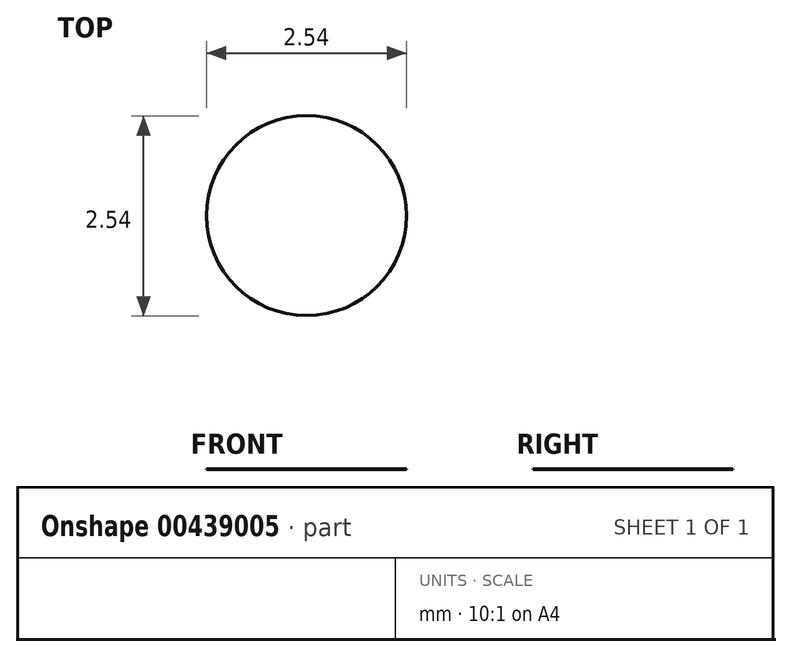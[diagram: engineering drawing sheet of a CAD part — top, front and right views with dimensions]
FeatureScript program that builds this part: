
annotation { "Feature Type Name" : "Feature", "Feature Type Description" : "" }
export const myFeature = defineFeature(function(context is Context, id is Id, definition is map)
    precondition{}
    {
        {
            var Q0;
            Q0=qCreatedBy(makeId("Top.planeOp"),FACE);
            var sketch = newSketch(context, id + "F0", { "sketchPlane" : qUnion([Q0])});
            skCircle(sketch, "E0.cCircle", {"center": v(0, 0) * mm, "radius": 44 * mm, "construction": true});
            skLineSegment(sketch, "E0.0", {"start": v(25.4, -44) * mm, "end": v(-25.4, -44) * mm});
            skLineSegment(sketch, "E0.1", {"start": v(-25.4, -44) * mm, "end": v(-50.8, 0) * mm});
            skLineSegment(sketch, "E0.2", {"start": v(-50.8, 0) * mm, "end": v(-25.4, 44) * mm, "construction": true});
            skLineSegment(sketch, "E0.3", {"start": v(-25.4, 44) * mm, "end": v(25.4, 44) * mm, "construction": true});
            skLineSegment(sketch, "E0.4", {"start": v(25.4, 44) * mm, "end": v(50.8, 0) * mm, "construction": true});
            skLineSegment(sketch, "E0.5", {"start": v(50.8, 0) * mm, "end": v(25.4, -44) * mm});
            skPoint(sketch, "E0.0.midPoint", {"position": v(0, -44) * mm});
            skCircle(sketch, "E1.cCircle", {"center": v(0, 87.99) * mm, "radius": 44 * mm, "construction": true});
            skLineSegment(sketch, "E1.0", {"start": v(25.4, 44) * mm, "end": v(-25.4, 44) * mm, "construction": true});
            skLineSegment(sketch, "E1.1", {"start": v(-25.4, 44) * mm, "end": v(-50.8, 87.99) * mm, "construction": true});
            skLineSegment(sketch, "E1.2", {"start": v(-50.8, 87.99) * mm, "end": v(-25.4, 131.98) * mm});
            skLineSegment(sketch, "E1.3", {"start": v(-25.4, 131.98) * mm, "end": v(25.4, 131.98) * mm});
            skLineSegment(sketch, "E1.4", {"start": v(25.4, 131.98) * mm, "end": v(50.8, 87.99) * mm});
            skLineSegment(sketch, "E1.5", {"start": v(50.8, 87.99) * mm, "end": v(25.4, 44) * mm, "construction": true});
            skPoint(sketch, "E1.0.midPoint", {"position": v(0, 44) * mm});
            skCircle(sketch, "E2.cCircle", {"center": v(76.2, 44) * mm, "radius": 44 * mm, "construction": true});
            skLineSegment(sketch, "E2.0", {"start": v(101.6, 0) * mm, "end": v(50.8, 0) * mm});
            skLineSegment(sketch, "E2.1", {"start": v(50.8, 0) * mm, "end": v(25.4, 44) * mm, "construction": true});
            skLineSegment(sketch, "E2.2", {"start": v(25.4, 44) * mm, "end": v(50.8, 87.99) * mm, "construction": true});
            skLineSegment(sketch, "E2.3", {"start": v(50.8, 87.99) * mm, "end": v(101.6, 87.99) * mm});
            skLineSegment(sketch, "E2.4", {"start": v(101.6, 87.99) * mm, "end": v(127, 44) * mm});
            skLineSegment(sketch, "E2.5", {"start": v(127, 44) * mm, "end": v(101.6, 0) * mm});
            skPoint(sketch, "E2.0.midPoint", {"position": v(76.2, 0) * mm});
            skCircle(sketch, "E3.cCircle", {"center": v(-76.2, 44) * mm, "radius": 44 * mm, "construction": true});
            skLineSegment(sketch, "E3.0", {"start": v(-50.8, 0) * mm, "end": v(-101.6, 0) * mm});
            skLineSegment(sketch, "E3.1", {"start": v(-101.6, 0) * mm, "end": v(-127, 44) * mm});
            skLineSegment(sketch, "E3.2", {"start": v(-127, 44) * mm, "end": v(-101.6, 87.99) * mm});
            skLineSegment(sketch, "E3.3", {"start": v(-101.6, 87.99) * mm, "end": v(-50.8, 87.99) * mm});
            skLineSegment(sketch, "E3.4", {"start": v(-50.8, 87.99) * mm, "end": v(-25.4, 44) * mm, "construction": true});
            skLineSegment(sketch, "E3.5", {"start": v(-25.4, 44) * mm, "end": v(-50.8, 0) * mm, "construction": true});
            skPoint(sketch, "E3.0.midPoint", {"position": v(-76.2, 0) * mm});
            skSolve(sketch);
        }
        {
            var Q0;
            Q0=makeQuery(id+"F0.imprint","IMPRINT",FACE,{"disambiguationData":[TD([[makeQuery(id+"F0.imprint","IMPRINT",EDGE,{"derivedFrom":sQuery(id+"F0.wireOp",EDGE,"E0.0")}),-1.0]])]});
            extrude(context, id + "F1", {"entities" : qUnion([Q0]), "depth" : 1 / 203.2 * mm});
        }
        {
            var Q0;
            Q0=makeQuery(id+"F1.opExtrude","CAP_FACE",FACE,{"disambiguationData":[OSD([sQuery(id+"F0.wireOp",EDGE,"E0.0"),sQuery(id+"F0.wireOp",EDGE,"E0.1"),sQuery(id+"F0.wireOp",EDGE,"E0.5"),sQuery(id+"F0.wireOp",EDGE,"E1.2"),sQuery(id+"F0.wireOp",EDGE,"E1.3"),sQuery(id+"F0.wireOp",EDGE,"E1.4"),sQuery(id+"F0.wireOp",EDGE,"E2.0"),sQuery(id+"F0.wireOp",EDGE,"E2.3"),sQuery(id+"F0.wireOp",EDGE,"E2.4"),sQuery(id+"F0.wireOp",EDGE,"E2.5"),sQuery(id+"F0.wireOp",EDGE,"E3.0"),sQuery(id+"F0.wireOp",EDGE,"E3.1"),sQuery(id+"F0.wireOp",EDGE,"E3.2"),sQuery(id+"F0.wireOp",EDGE,"E3.3")])],"isStart":false});
            var sketch = newSketch(context, id + "F2", { "sketchPlane" : qUnion([Q0])});
            skLineSegment(sketch, "E4", {"start": v(-50.8, 87.99) * mm, "end": v(-50.8, 0) * mm, "construction": true});
            skLineSegment(sketch, "E5", {"start": v(25.4, 131.98) * mm, "end": v(-25.4, 131.98) * mm, "construction": true});
            skPoint(sketch, "E6", {"position": v(-21.6, 69.4) * mm});
            skLineSegment(sketch, "E7.bottom", {"start": v(-20, 56.7) * mm, "end": v(-23.18, 56.7) * mm});
            skLineSegment(sketch, "E7.top", {"start": v(-20, 82.1) * mm, "end": v(-23.18, 82.1) * mm});
            skLineSegment(sketch, "E7.left", {"start": v(-20, 56.7) * mm, "end": v(-20, 82.1) * mm});
            skLineSegment(sketch, "E7.right", {"start": v(-23.18, 56.7) * mm, "end": v(-23.18, 82.1) * mm});
            skPoint(sketch, "E8", {"position": v(-21.59, 18.6) * mm});
            skLineSegment(sketch, "E9.bottom", {"start": v(-20, 5.9) * mm, "end": v(-23.18, 5.9) * mm});
            skLineSegment(sketch, "E9.top", {"start": v(-20, 31.3) * mm, "end": v(-23.18, 31.3) * mm});
            skLineSegment(sketch, "E9.left", {"start": v(-20, 5.9) * mm, "end": v(-20, 31.3) * mm});
            skLineSegment(sketch, "E9.right", {"start": v(-23.18, 5.9) * mm, "end": v(-23.18, 31.3) * mm});
            skLineSegment(sketch, "E10", {"start": v(0, 131.98) * mm, "end": v(0, -44) * mm, "construction": true});
            skLineSegment(sketch, "E11.MirrorCS", {"start": v(20, 82.1) * mm, "end": v(23.18, 82.1) * mm});
            skLineSegment(sketch, "E12.MirrorCS", {"start": v(20, 56.7) * mm, "end": v(20, 82.1) * mm});
            skLineSegment(sketch, "E13.MirrorCS", {"start": v(23.18, 56.7) * mm, "end": v(23.18, 82.1) * mm});
            skLineSegment(sketch, "E14.MirrorCS", {"start": v(20, 56.7) * mm, "end": v(23.18, 56.7) * mm});
            skLineSegment(sketch, "E15.MirrorCS", {"start": v(20, 31.3) * mm, "end": v(23.18, 31.3) * mm});
            skLineSegment(sketch, "E16.MirrorCS", {"start": v(20, 5.9) * mm, "end": v(20, 31.3) * mm});
            skLineSegment(sketch, "E17.MirrorCS", {"start": v(20, 5.9) * mm, "end": v(23.18, 5.9) * mm});
            skLineSegment(sketch, "E18.MirrorCS", {"start": v(23.18, 5.9) * mm, "end": v(23.18, 31.3) * mm});
            skPoint(sketch, "E19", {"position": v(-21.6, 44) * mm});
            skCircle(sketch, "E20", {"center": v(-21.6, 44) * mm, "radius": 1.27 * mm});
            skCircle(sketch, "E21.MirrorC", {"center": v(21.59, 44) * mm, "radius": 1.27 * mm});
            skLineSegment(sketch, "E22", {"start": v(-21.6, 131.98) * mm, "end": v(-21.59, -44) * mm, "construction": true});
            skLineSegment(sketch, "E23", {"start": v(99.38, 6.75) * mm, "end": v(99.38, 29.94) * mm, "construction": true});
            skSolve(sketch);
        }
        {
            var Q0;
            Q0=makeQuery(id+"F2.imprint","IMPRINT",FACE,{"disambiguationData":[TD([[makeQuery(id+"F2.imprint","IMPRINT",EDGE,{"derivedFrom":sQuery(id+"F2.wireOp",EDGE,"E7.bottom")}),-1.0]])]});
            var Q1;
            Q1=makeQuery(id+"F2.imprint","IMPRINT",FACE,{"disambiguationData":[TD([[makeQuery(id+"F2.imprint","IMPRINT",EDGE,{"derivedFrom":sQuery(id+"F2.wireOp",EDGE,"E11.MirrorCS")}),-1.0]])]});
            var Q2;
            Q2=makeQuery(id+"F2.imprint","IMPRINT",FACE,{"disambiguationData":[TD([[makeQuery(id+"F2.imprint","IMPRINT",EDGE,{"derivedFrom":sQuery(id+"F2.wireOp",EDGE,"E15.MirrorCS")}),-1.0]])]});
            var Q3;
            Q3=makeQuery(id+"F2.imprint","IMPRINT",FACE,{"disambiguationData":[TD([[makeQuery(id+"F2.imprint","IMPRINT",EDGE,{"derivedFrom":sQuery(id+"F2.wireOp",EDGE,"E9.bottom")}),-1.0]])]});
            extrude(context, id + "F3", {"entities" : qUnion([Q0, Q1, Q2, Q3]), "operationType" : NewBodyOperationType.REMOVE, "oppositeDirection" : true, "depth" : 7.62 * mm});
        }
        {
            var Q0;
            Q0=makeQuery(id+"F2.imprint","IMPRINT",FACE,{"disambiguationData":[TD([[makeQuery(id+"F2.imprint","IMPRINT",EDGE,{"derivedFrom":sQuery(id+"F2.wireOp",EDGE,"E20")}),1.0]])]});
            var Q1;
            Q1=makeQuery(id+"F2.imprint","IMPRINT",FACE,{"disambiguationData":[TD([[makeQuery(id+"F2.imprint","IMPRINT",EDGE,{"derivedFrom":sQuery(id+"F2.wireOp",EDGE,"E21.MirrorC")}),-1.0]])]});
            extrude(context, id + "F4", {"entities" : qUnion([Q0, Q1]), "operationType" : NewBodyOperationType.REMOVE, "oppositeDirection" : true, "depth" : 7.62 * mm});
        }
        {
            var Q0;
            Q0=makeQuery(id+"F2.imprint","IMPRINT",FACE,{"disambiguationData":[TD([[makeQuery(id+"F2.imprint","IMPRINT",EDGE,{"derivedFrom":sQuery(id+"F2.wireOp",EDGE,"E7.bottom")}),1.0]])]});
            var sketch = newSketch(context, id + "F5", { "sketchPlane" : qUnion([Q0])});
            skCircle(sketch, "E24", {"center": v(97.8, 21.95) * mm, "radius": 2.15 * mm});
            skPoint(sketch, "E25.0", {"position": v(21.59, 44) * mm});
            skPoint(sketch, "E26.0", {"position": v(127, 44) * mm});
            skLineSegment(sketch, "E27", {"start": v(21.59, 44) * mm, "end": v(127, 44) * mm, "construction": true});
            skCircle(sketch, "E28.MirrorC", {"center": v(97.8, 66.04) * mm, "radius": 2.15 * mm});
            skPoint(sketch, "E29.0", {"position": v(0, -44) * mm});
            skPoint(sketch, "E29.1", {"position": v(0, 131.98) * mm});
            skLineSegment(sketch, "E30", {"start": v(0, -44) * mm, "end": v(0, 131.98) * mm, "construction": true});
            skCircle(sketch, "E31.MirrorC", {"center": v(-97.8, 66.04) * mm, "radius": 2.15 * mm});
            skSolve(sketch);
        }
        {
            var Q0;
            Q0=makeQuery(id+"F5.imprint","IMPRINT",FACE,{"disambiguationData":[TD([[makeQuery(id+"F5.imprint","IMPRINT",EDGE,{"derivedFrom":sQuery(id+"F5.wireOp",EDGE,"E28.MirrorC")}),-1.0]])]});
            var Q1;
            Q1=makeQuery(id+"F5.imprint","IMPRINT",FACE,{"disambiguationData":[TD([[makeQuery(id+"F5.imprint","IMPRINT",EDGE,{"derivedFrom":sQuery(id+"F5.wireOp",EDGE,"E31.MirrorC")}),1.0]])]});
            extrude(context, id + "F6", {"entities" : qUnion([Q0, Q1]), "operationType" : NewBodyOperationType.REMOVE, "oppositeDirection" : true, "depth" : 25.4 * mm, "offsetDistance" : 25.4 * mm});
        }
    });
